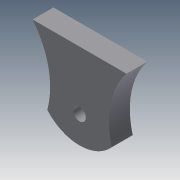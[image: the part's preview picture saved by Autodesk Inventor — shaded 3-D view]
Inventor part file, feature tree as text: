
AUTODESK INVENTOR PART (.ipt)
format: ipt  version: 2013 (Build 170138000, 138)  size: 79,872 bytes
history: native  units: mm
features: extrude x1, sketch x1
ambient origin geometry x8: Origin, YZ Plane, XZ Plane, XY Plane, X Axis, Y Axis, Z Axis, Center Point
bodies: Solid1 (feature_tree)
feature tree (2):
  extrude  "Extrusion1"  Depth=10.0mm TaperAngle=0.0deg
  sketch  "Sketch1"  dims[d0=6.0mm d1=38.0mm d2=38.0mm d3=41.0mm d4=45.0mm d5=10.0mm d6=0.0mm]
